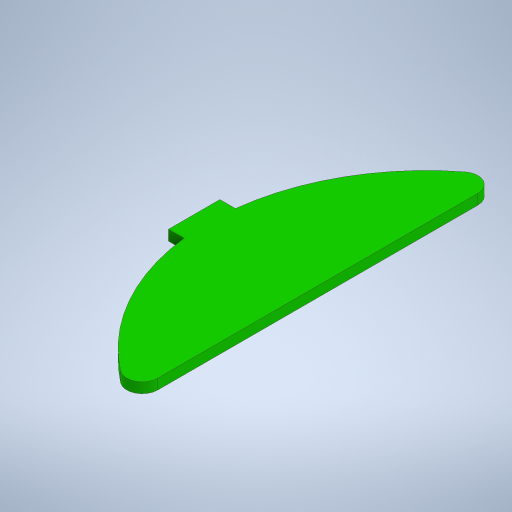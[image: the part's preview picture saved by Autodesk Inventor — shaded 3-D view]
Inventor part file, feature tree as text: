
AUTODESK INVENTOR PART (.ipt)
format: ipt  version: 2024 (Build 280153000, 153)  size: 237,568 bytes
history: native  units: mm
features: extrude x1, fillet x1, sketch x1
ambient origin geometry x8: Origin, YZ Plane, XZ Plane, XY Plane, X Axis, Y Axis, Z Axis, Center Point
bodies: Solide1 (feature_tree)
feature tree (3):
  extrude  "Extrusion1"  Depth=2.0mm TaperAngle=0.0deg
  fillet  "Congé2"  Radius=3.0mm
  sketch  "Esquisse1"
